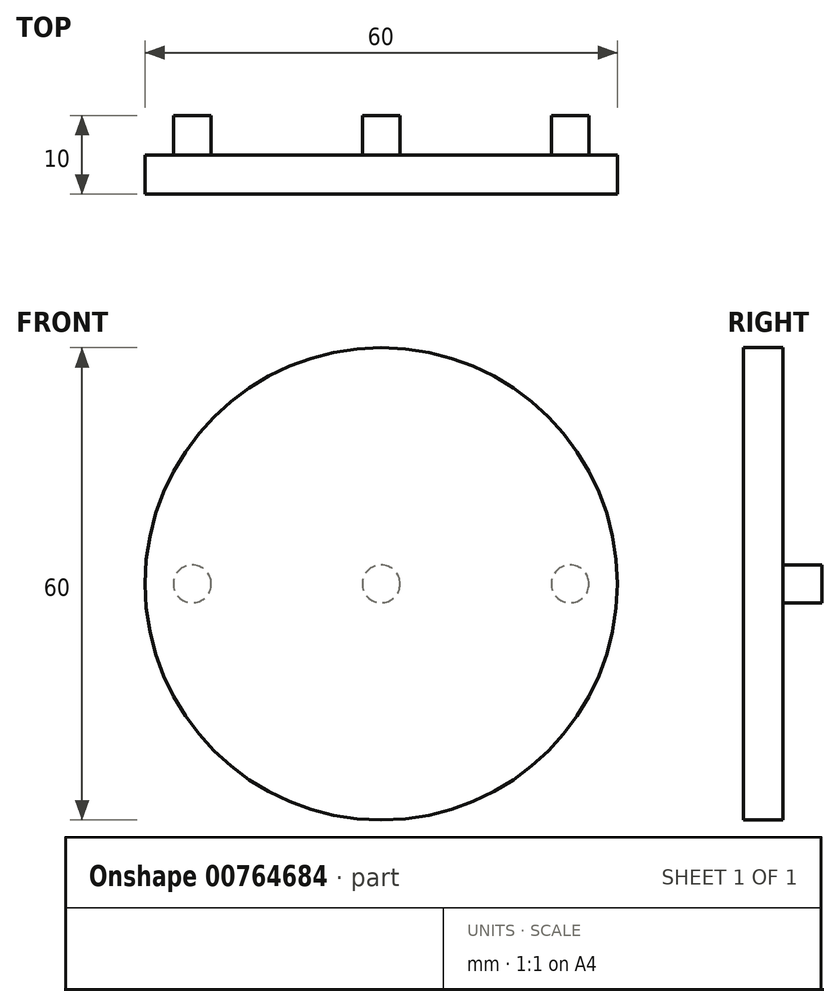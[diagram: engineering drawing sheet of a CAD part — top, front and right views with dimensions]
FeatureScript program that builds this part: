
annotation { "Feature Type Name" : "Feature", "Feature Type Description" : "" }
export const myFeature = defineFeature(function(context is Context, id is Id, definition is map)
    precondition{}
    {
        {
            var Q0;
            Q0=qCreatedBy(makeId("Front.planeOp"),FACE);
            var sketch = newSketch(context, id + "F0", { "sketchPlane" : qUnion([Q0])});
            skCircle(sketch, "E0", {"center": v(0, 0) * mm, "radius": 2.4 * mm});
            skCircle(sketch, "E1", {"center": v(-24, 0) * mm, "radius": 2.4 * mm});
            skCircle(sketch, "E2", {"center": v(24, 0) * mm, "radius": 2.4 * mm});
            skSolve(sketch);
        }
        {
            var Q0;
            Q0=qCreatedBy(makeId("Front.planeOp"),FACE);
            var sketch = newSketch(context, id + "F1", { "sketchPlane" : qUnion([Q0])});
            skCircle(sketch, "E3", {"center": v(0, 0) * mm, "radius": 30 * mm});
            skSolve(sketch);
        }
        {
            var Q0;
            Q0=makeQuery(id+"F1.imprint","IMPRINT",FACE,{"disambiguationData":[TD([[makeQuery(id+"F1.imprint","IMPRINT",EDGE,{"derivedFrom":sQuery(id+"F1.wireOp",EDGE,"E3")}),1.0]])]});
            extrude(context, id + "F2", {"entities" : qUnion([Q0]), "depth" : 5 * mm, "offsetDistance" : 25 * mm});
        }
        {
            var Q0;
            Q0 = qSketchRegion(id + "F0", true);
            extrude(context, id + "F3", {"entities" : qUnion([Q0]), "operationType" : NewBodyOperationType.ADD, "oppositeDirection" : true, "depth" : 5 * mm, "offsetDistance" : 25 * mm});
        }
    });
